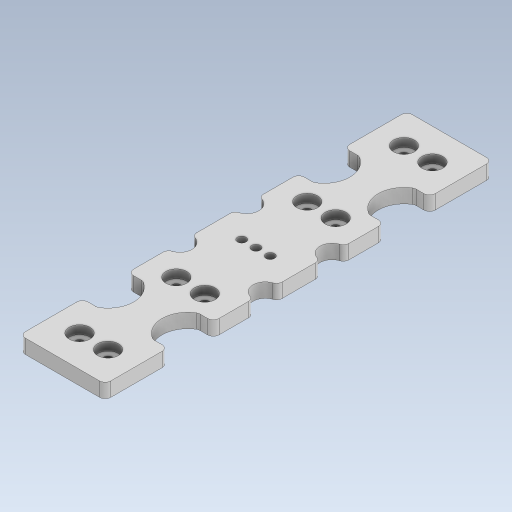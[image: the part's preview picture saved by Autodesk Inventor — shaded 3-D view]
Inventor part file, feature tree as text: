
AUTODESK INVENTOR PART (.ipt)
format: ipt  version: 2023.5 (Build 275446000, 446)  size: 252,416 bytes
history: native  units: mm
features: extrude x2, sketch x1
ambient origin geometry x8: Origin, YZ Plane, XZ Plane, XY Plane, X Axis, Y Axis, Z Axis, Center Point
bodies: Solid1 (feature_tree)
feature tree (3):
  sketch  "Sketch1"  dims[d0=15.0mm d1=7.5mm d2=7.3mm d3=23.0mm d4=10.0mm d5=7.3mm d6=10.0mm d7=34.0mm d8=4.0mm d9=4.0mm d10=2.0mm d11=2.0mm d12=2.0mm d13=2.0mm d14=2.0mm d15=5.0mm d16=0.0mm d17=2.0mm d18=0.0mm d19=3.0mm d20=3.0mm d21=3.0mm d22=3.0mm d23=3.0mm d24=3.0mm d25=3.0mm d26=3.0mm d27=3.0mm d28=3.0mm d29=3.0mm]
  extrude  "Extrusion1"  Depth=5.0mm TaperAngle=0.0deg
  extrude  "Extrusion2"  Depth=2.0mm TaperAngle=0.0deg
